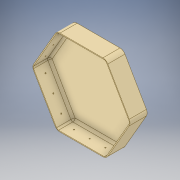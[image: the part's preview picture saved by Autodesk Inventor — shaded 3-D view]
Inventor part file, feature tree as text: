
AUTODESK INVENTOR PART (.ipt)
format: ipt  version: 2019 (Build 230136000, 136)  size: 192,000 bytes
history: native  units: mm
features: mirror x4, plane x3, other x3, extrude x2, sketch x2, fillet x2, shell x1, projected_geometry x1
ambient origin geometry x8: Origin, YZ Plane, XZ Plane, XY Plane, X Axis, Y Axis, Z Axis, Center Point
bodies: Solid1 (feature_tree)
feature tree (18):
  extrude  "Extrusion1"  Depth=30.0mm TaperAngle=0.0deg
  shell  "Shell1"  Thickness=1.5mm
  sketch  "Sketch2"  dims[d5=2.0mm d6=15.0mm d7=15.0mm d8=1.0mm d9=0.0mm d10=4.0mm d11=10.0mm d12=1.0mm]
  plane  "Work Plane1"
  plane  "Work Plane2"
  plane  "Work Plane3"
  extrude  "Extrusion2"  Depth=1.0mm
  mirror  "Mirror1"
  mirror  "Mirror2"
  mirror  "Mirror3"
  mirror  "Mirror4"
  fillet  "Fillet1"  Radius=15.0mm
  fillet  "Fillet2"  Radius=1.0mm
  other  "Work Axis1"
  other  "Work Axis2"
  other  "Work Axis3"
  sketch  "Sketch1"  dims[d0=150.0mm d2=30.0mm d3=0.0mm d4=1.5mm]
  projected_geometry  "Projected Loop1"
